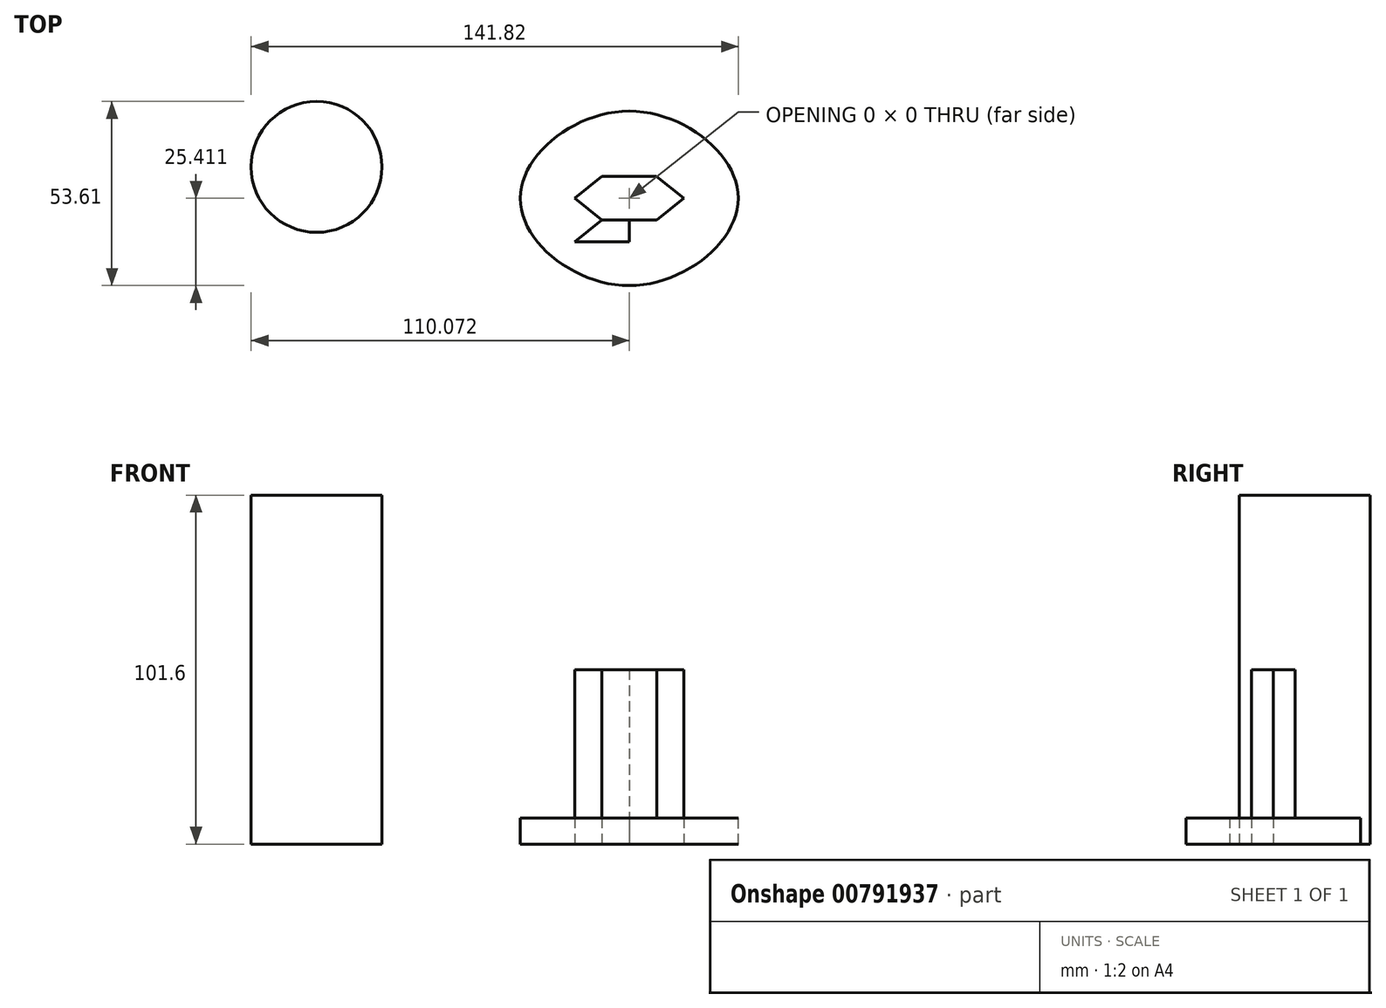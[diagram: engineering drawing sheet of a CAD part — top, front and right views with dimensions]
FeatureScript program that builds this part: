
annotation { "Feature Type Name" : "Feature", "Feature Type Description" : "" }
export const myFeature = defineFeature(function(context is Context, id is Id, definition is map)
    precondition{}
    {
        {
            var Q0;
            Q0=qCreatedBy(makeId("Top.planeOp"),FACE);
            var sketch = newSketch(context, id + "F0", { "sketchPlane" : qUnion([Q0])});
            skCircle(sketch, "E0", {"center": v(-43.44, 15.51) * mm, "radius": 19.05 * mm});
            skFitSpline(sketch, "E1", {"points": [v(15.83, 6.35) * mm, v(47.6, 31.75) * mm, v(79.33, 6.38) * mm, v(47.56, -19.05) * mm, v(15.83, 6.35) * mm]});
            skLineSegment(sketch, "E2", {"start": v(47.6, 31.75) * mm, "end": v(47.56, -19.05) * mm});
            skLineSegment(sketch, "E3", {"start": v(15.83, 6.35) * mm, "end": v(79.33, 6.38) * mm});
            skLineSegment(sketch, "E4", {"start": v(79.33, 6.38) * mm, "end": v(47.56, -19.05) * mm});
            skLineSegment(sketch, "E5", {"start": v(47.56, -19.05) * mm, "end": v(15.83, 6.35) * mm});
            skLineSegment(sketch, "E6", {"start": v(15.83, 6.35) * mm, "end": v(47.6, 31.75) * mm});
            skLineSegment(sketch, "E7", {"start": v(79.33, 6.38) * mm, "end": v(47.6, 31.75) * mm});
            skLineSegment(sketch, "E8", {"start": v(47.58, 6.36) * mm, "end": v(63.46, 19.06) * mm});
            skLineSegment(sketch, "E9", {"start": v(63.46, 19.06) * mm, "end": v(63.45, -6.34) * mm});
            skLineSegment(sketch, "E10", {"start": v(63.45, -6.34) * mm, "end": v(47.58, 6.36) * mm});
            skLineSegment(sketch, "E11", {"start": v(47.58, 6.36) * mm, "end": v(31.71, 19.05) * mm});
            skLineSegment(sketch, "E12", {"start": v(31.71, 19.05) * mm, "end": v(31.7, -6.35) * mm});
            skLineSegment(sketch, "E13", {"start": v(31.7, -6.35) * mm, "end": v(63.45, -6.34) * mm});
            skLineSegment(sketch, "E14", {"start": v(47.58, 6.36) * mm, "end": v(31.7, -6.35) * mm});
            skLineSegment(sketch, "E15", {"start": v(63.46, 19.06) * mm, "end": v(31.71, 19.05) * mm});
            skLineSegment(sketch, "E16", {"start": v(31.7, 6.35) * mm, "end": v(39.65, 12.7) * mm});
            skLineSegment(sketch, "E17", {"start": v(39.65, 12.7) * mm, "end": v(47.59, 12.7) * mm});
            skLineSegment(sketch, "E18", {"start": v(47.59, 12.7) * mm, "end": v(55.52, 12.71) * mm});
            skLineSegment(sketch, "E19", {"start": v(55.52, 12.71) * mm, "end": v(63.46, 6.36) * mm});
            skLineSegment(sketch, "E20", {"start": v(63.46, 6.36) * mm, "end": v(55.53, 0) * mm});
            skLineSegment(sketch, "E21", {"start": v(55.53, 0) * mm, "end": v(39.63, 0) * mm});
            skLineSegment(sketch, "E22", {"start": v(39.63, 0) * mm, "end": v(47.58, 0) * mm});
            skLineSegment(sketch, "E23", {"start": v(47.58, 0) * mm, "end": v(39.63, 0) * mm});
            skLineSegment(sketch, "E24", {"start": v(31.7, 6.35) * mm, "end": v(39.63, 0) * mm});
            skSolve(sketch);
        }
        {
            var Q0;
            Q0=makeQuery(id+"F0.imprint","IMPRINT",FACE,{"disambiguationData":[TD([[makeQuery(id+"F0.imprint","IMPRINT",EDGE,{"derivedFrom":sQuery(id+"F0.wireOp",EDGE,"E0")}),1.0]])]});
            extrude(context, id + "F1", {"entities" : qUnion([Q0]), "depth" : 101.6 * mm, "offsetDistance" : 25.4 * mm});
        }
        {
            var Q0;
            Q0=makeQuery(id+"F0.imprint","IMPRINT",FACE,{"disambiguationData":[TD([[makeQuery(id+"F0.imprint","IMPRINT",EDGE,{"derivedFrom":sQuery(id+"F0.wireOp",EDGE,"E1")}),-1.0]])]});
            var Q1;
            {var subQ1=sQuery(id+"F0.wireOp",EDGE,"E3");var subQ3=sQuery(id+"F0.wireOp",EDGE,"E12");var subQ4=makeQuery(id+"F0.imprint","INTERSECT",VERTEX,{"derivedFrom":[subQ1,subQ3]});Q1=makeQuery(id+"F0.imprint","IMPRINT",FACE,{"disambiguationData":[TD([[makeQuery(id+"F0.imprint","IMPRINT",EDGE,{"disambiguationData":[TD([[subQ4,-1.0]])],"derivedFrom":subQ3}),-1.0]])]});}
            var Q2;
            {var subQ1=sQuery(id+"F0.wireOp",EDGE,"E3");var subQ3=sQuery(id+"F0.wireOp",EDGE,"E12");var subQ4=makeQuery(id+"F0.imprint","INTERSECT",VERTEX,{"derivedFrom":[subQ1,subQ3]});Q2=makeQuery(id+"F0.imprint","IMPRINT",FACE,{"disambiguationData":[TD([[makeQuery(id+"F0.imprint","IMPRINT",EDGE,{"disambiguationData":[TD([[subQ4,1.0]])],"derivedFrom":subQ1}),1.0]])]});}
            var Q3;
            {var subQ0=sQuery(id+"F0.wireOp",EDGE,"E12");var subQ1=sQuery(id+"F0.wireOp",EDGE,"E3");var subQ2=makeQuery(id+"F0.imprint","INTERSECT",VERTEX,{"derivedFrom":[subQ1,subQ0]});Q3=makeQuery(id+"F0.imprint","IMPRINT",FACE,{"disambiguationData":[TD([[makeQuery(id+"F0.imprint","IMPRINT",EDGE,{"disambiguationData":[TD([[subQ2,-1.0]])],"derivedFrom":subQ1}),1.0]])]});}
            var Q4;
            {var subQ0=sQuery(id+"F0.wireOp",EDGE,"E17");Q4=makeQuery(id+"F0.imprint","IMPRINT",FACE,{"disambiguationData":[TD([[makeQuery(id+"F0.imprint","IMPRINT",EDGE,{"derivedFrom":subQ0}),1.0]])]});}
            var Q5;
            {var subQ1=sQuery(id+"F0.wireOp",EDGE,"E2");var subQ3=sQuery(id+"F0.wireOp",EDGE,"E15");var subQ4=makeQuery(id+"F0.imprint","INTERSECT",VERTEX,{"derivedFrom":[subQ1,subQ3]});Q5=makeQuery(id+"F0.imprint","IMPRINT",FACE,{"disambiguationData":[TD([[makeQuery(id+"F0.imprint","IMPRINT",EDGE,{"disambiguationData":[TD([[subQ4,1.0]])],"derivedFrom":subQ1}),-1.0]])]});}
            var Q6;
            {var subQ1=sQuery(id+"F0.wireOp",EDGE,"E2");var subQ3=sQuery(id+"F0.wireOp",EDGE,"E15");var subQ4=makeQuery(id+"F0.imprint","INTERSECT",VERTEX,{"derivedFrom":[subQ1,subQ3]});Q6=makeQuery(id+"F0.imprint","IMPRINT",FACE,{"disambiguationData":[TD([[makeQuery(id+"F0.imprint","IMPRINT",EDGE,{"disambiguationData":[TD([[subQ4,1.0]])],"derivedFrom":subQ1}),1.0]])]});}
            var Q7;
            {var subQ0=sQuery(id+"F0.wireOp",EDGE,"E18");Q7=makeQuery(id+"F0.imprint","IMPRINT",FACE,{"disambiguationData":[TD([[makeQuery(id+"F0.imprint","IMPRINT",EDGE,{"derivedFrom":subQ0}),1.0]])]});}
            var Q8;
            {var subQ0=sQuery(id+"F0.wireOp",EDGE,"E19");var subQ1=sQuery(id+"F0.wireOp",EDGE,"E3");var subQ2=makeQuery(id+"F0.imprint","INTERSECT",VERTEX,{"derivedFrom":[subQ1,subQ0]});Q8=makeQuery(id+"F0.imprint","IMPRINT",FACE,{"disambiguationData":[TD([[makeQuery(id+"F0.imprint","IMPRINT",EDGE,{"disambiguationData":[TD([[subQ2,-1.0]])],"derivedFrom":subQ1}),1.0]])]});}
            var Q9;
            {var subQ1=sQuery(id+"F0.wireOp",EDGE,"E3");var subQ3=sQuery(id+"F0.wireOp",EDGE,"E9");var subQ4=makeQuery(id+"F0.imprint","INTERSECT",VERTEX,{"derivedFrom":[subQ1,subQ3]});Q9=makeQuery(id+"F0.imprint","IMPRINT",FACE,{"disambiguationData":[TD([[makeQuery(id+"F0.imprint","IMPRINT",EDGE,{"disambiguationData":[TD([[subQ4,-1.0]])],"derivedFrom":subQ1}),1.0]])]});}
            var Q10;
            {var subQ1=sQuery(id+"F0.wireOp",EDGE,"E3");var subQ3=sQuery(id+"F0.wireOp",EDGE,"E9");var subQ4=makeQuery(id+"F0.imprint","INTERSECT",VERTEX,{"derivedFrom":[subQ1,subQ3]});Q10=makeQuery(id+"F0.imprint","IMPRINT",FACE,{"disambiguationData":[TD([[makeQuery(id+"F0.imprint","IMPRINT",EDGE,{"disambiguationData":[TD([[subQ4,-1.0]])],"derivedFrom":subQ3}),1.0]])]});}
            var Q11;
            {var subQ3=sQuery(id+"F0.wireOp",EDGE,"E20");Q11=makeQuery(id+"F0.imprint","IMPRINT",FACE,{"disambiguationData":[TD([[makeQuery(id+"F0.imprint","IMPRINT",EDGE,{"derivedFrom":subQ3}),1.0]])]});}
            var Q12;
            {var subQ0=sQuery(id+"F0.wireOp",EDGE,"E21");Q12=makeQuery(id+"F0.imprint","IMPRINT",FACE,{"disambiguationData":[TD([[makeQuery(id+"F0.imprint","IMPRINT",EDGE,{"derivedFrom":subQ0}),1.0]])]});}
            var Q13;
            {var subQ1=sQuery(id+"F0.wireOp",EDGE,"E2");var subQ3=sQuery(id+"F0.wireOp",EDGE,"E13");var subQ4=makeQuery(id+"F0.imprint","INTERSECT",VERTEX,{"derivedFrom":[subQ1,subQ3]});Q13=makeQuery(id+"F0.imprint","IMPRINT",FACE,{"disambiguationData":[TD([[makeQuery(id+"F0.imprint","IMPRINT",EDGE,{"disambiguationData":[TD([[subQ4,-1.0]])],"derivedFrom":subQ1}),1.0]])]});}
            var Q14;
            {var subQ1=sQuery(id+"F0.wireOp",EDGE,"E2");var subQ3=sQuery(id+"F0.wireOp",EDGE,"E13");var subQ4=makeQuery(id+"F0.imprint","INTERSECT",VERTEX,{"derivedFrom":[subQ1,subQ3]});Q14=makeQuery(id+"F0.imprint","IMPRINT",FACE,{"disambiguationData":[TD([[makeQuery(id+"F0.imprint","IMPRINT",EDGE,{"disambiguationData":[TD([[subQ4,-1.0]])],"derivedFrom":subQ1}),-1.0]])]});}
            var Q15;
            {var subQ0=sQuery(id+"F0.wireOp",EDGE,"E23");var subQ1=sQuery(id+"F0.wireOp",EDGE,"E2");var subQ2=makeQuery(id+"F0.imprint","INTERSECT",VERTEX,{"derivedFrom":[subQ1,subQ0]});Q15=makeQuery(id+"F0.imprint","IMPRINT",FACE,{"disambiguationData":[TD([[makeQuery(id+"F0.imprint","IMPRINT",EDGE,{"disambiguationData":[TD([[subQ2,-1.0]])],"derivedFrom":subQ1}),-1.0]])]});}
            var Q16;
            {var subQ3=sQuery(id+"F0.wireOp",EDGE,"E24");Q16=makeQuery(id+"F0.imprint","IMPRINT",FACE,{"disambiguationData":[TD([[makeQuery(id+"F0.imprint","IMPRINT",EDGE,{"derivedFrom":subQ3}),-1.0]])]});}
            extrude(context, id + "F2", {"entities" : qUnion([Q0, Q1, Q2, Q3, Q4, Q5, Q6, Q7, Q8, Q9, Q10, Q11, Q12, Q13, Q14, Q15, Q16]), "depth" : 7.62 * mm, "offsetDistance" : 25.4 * mm});
        }
        {
            var Q0;
            {var subQ0=sQuery(id+"F0.wireOp",EDGE,"E17");Q0=makeQuery(id+"F0.imprint","IMPRINT",FACE,{"disambiguationData":[TD([[makeQuery(id+"F0.imprint","IMPRINT",EDGE,{"derivedFrom":subQ0}),-1.0]])]});}
            var Q1;
            {var subQ0=sQuery(id+"F0.wireOp",EDGE,"E18");Q1=makeQuery(id+"F0.imprint","IMPRINT",FACE,{"disambiguationData":[TD([[makeQuery(id+"F0.imprint","IMPRINT",EDGE,{"derivedFrom":subQ0}),-1.0]])]});}
            var Q2;
            {var subQ1=sQuery(id+"F0.wireOp",EDGE,"E3");var subQ3=sQuery(id+"F0.wireOp",EDGE,"E19");var subQ4=makeQuery(id+"F0.imprint","INTERSECT",VERTEX,{"derivedFrom":[subQ1,subQ3]});Q2=makeQuery(id+"F0.imprint","IMPRINT",FACE,{"disambiguationData":[TD([[makeQuery(id+"F0.imprint","IMPRINT",EDGE,{"disambiguationData":[TD([[subQ4,1.0]])],"derivedFrom":subQ3}),-1.0]])]});}
            var Q3;
            {var subQ5=sQuery(id+"F0.wireOp",EDGE,"E20");Q3=makeQuery(id+"F0.imprint","IMPRINT",FACE,{"disambiguationData":[TD([[makeQuery(id+"F0.imprint","IMPRINT",EDGE,{"derivedFrom":subQ5}),-1.0]])]});}
            var Q4;
            {var subQ7=sQuery(id+"F0.wireOp",EDGE,"E21");Q4=makeQuery(id+"F0.imprint","IMPRINT",FACE,{"disambiguationData":[TD([[makeQuery(id+"F0.imprint","IMPRINT",EDGE,{"derivedFrom":subQ7}),-1.0]])]});}
            var Q5;
            {var subQ0=sQuery(id+"F0.wireOp",EDGE,"E14");var subQ1=sQuery(id+"F0.wireOp",EDGE,"E2");var subQ2=makeQuery(id+"F0.imprint","INTERSECT",VERTEX,{"derivedFrom":[subQ1,subQ0]});Q5=makeQuery(id+"F0.imprint","IMPRINT",FACE,{"disambiguationData":[TD([[makeQuery(id+"F0.imprint","IMPRINT",EDGE,{"disambiguationData":[TD([[subQ2,-1.0]])],"derivedFrom":subQ1}),-1.0]])]});}
            var Q6;
            {var subQ0=sQuery(id+"F0.wireOp",EDGE,"E24");Q6=makeQuery(id+"F0.imprint","IMPRINT",FACE,{"disambiguationData":[TD([[makeQuery(id+"F0.imprint","IMPRINT",EDGE,{"derivedFrom":subQ0}),1.0]])]});}
            var Q7;
            {var subQ0=sQuery(id+"F0.wireOp",EDGE,"E11");var subQ1=sQuery(id+"F0.wireOp",EDGE,"E2");var subQ2=makeQuery(id+"F0.imprint","INTERSECT",VERTEX,{"derivedFrom":[subQ1,subQ0]});Q7=makeQuery(id+"F0.imprint","IMPRINT",FACE,{"disambiguationData":[TD([[makeQuery(id+"F0.imprint","IMPRINT",EDGE,{"disambiguationData":[TD([[subQ2,-1.0]])],"derivedFrom":subQ1}),-1.0]])]});}
            extrude(context, id + "F3", {"entities" : qUnion([Q0, Q1, Q2, Q3, Q4, Q5, Q6, Q7]), "operationType" : NewBodyOperationType.ADD, "depth" : 50.8 * mm, "offsetDistance" : 25.4 * mm});
        }
    });
